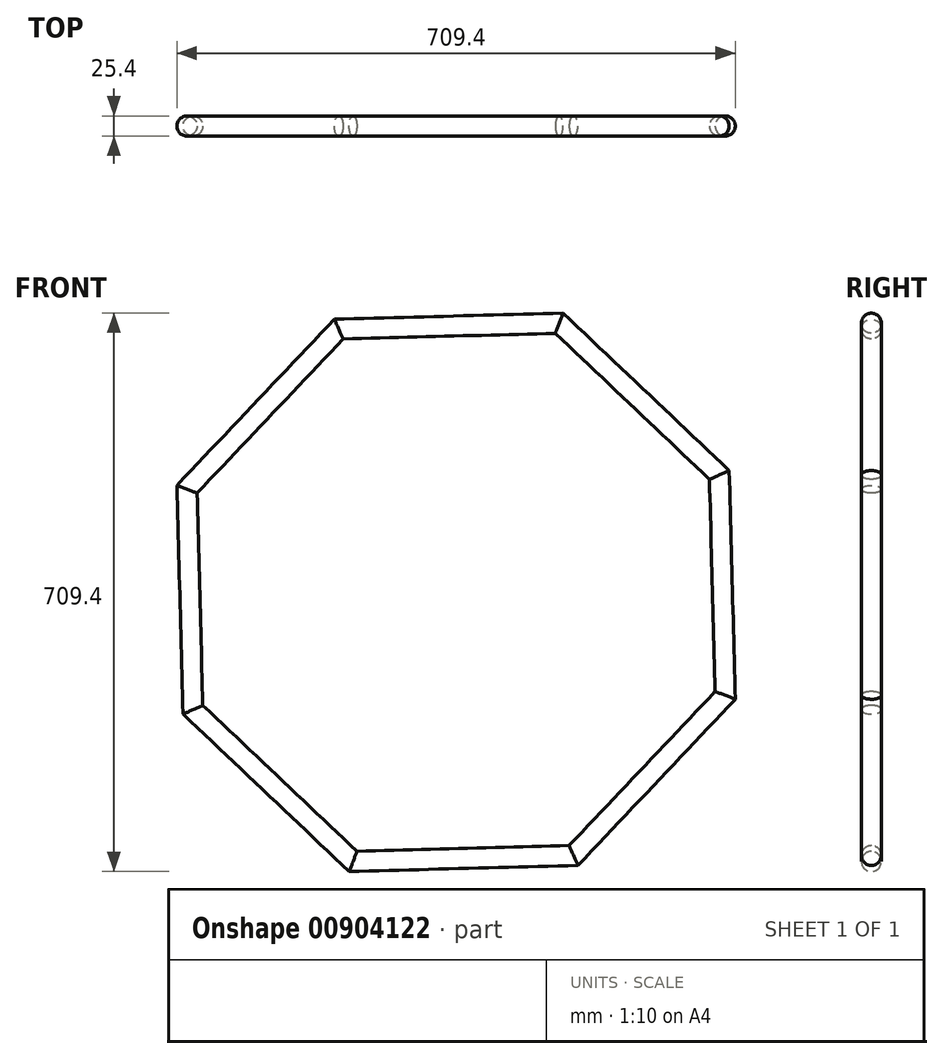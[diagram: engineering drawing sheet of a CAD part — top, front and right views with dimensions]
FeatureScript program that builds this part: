
annotation { "Feature Type Name" : "Feature", "Feature Type Description" : "" }
export const myFeature = defineFeature(function(context is Context, id is Id, definition is map)
    precondition{}
    {
        {
            var Q0;
            Q0=qCreatedBy(makeId("Front.planeOp"),FACE);
            var sketch = newSketch(context, id + "F0", { "sketchPlane" : qUnion([Q0])});
            skLineSegment(sketch, "E0.bottom", {"start": v(304.8, 304.8) * mm, "end": v(-304.8, 304.8) * mm});
            skLineSegment(sketch, "E0.top", {"start": v(304.8, -304.8) * mm, "end": v(-304.8, -304.8) * mm});
            skLineSegment(sketch, "E0.left", {"start": v(304.8, 304.8) * mm, "end": v(304.8, -304.8) * mm});
            skLineSegment(sketch, "E0.right", {"start": v(-304.8, 304.8) * mm, "end": v(-304.8, -304.8) * mm});
            skPoint(sketch, "E0.middle", {"position": v(0, 0) * mm});
            skCircle(sketch, "E1.cCircle", {"center": v(0, 0) * mm, "radius": 337.27 * mm, "construction": true});
            skLineSegment(sketch, "E1.0", {"start": v(333.4, 148.71) * mm, "end": v(340.9, -130.59) * mm});
            skLineSegment(sketch, "E1.1", {"start": v(340.9, -130.59) * mm, "end": v(148.71, -333.4) * mm});
            skLineSegment(sketch, "E1.2", {"start": v(148.71, -333.4) * mm, "end": v(-130.59, -340.9) * mm});
            skLineSegment(sketch, "E1.3", {"start": v(-130.59, -340.9) * mm, "end": v(-333.4, -148.71) * mm});
            skLineSegment(sketch, "E1.4", {"start": v(-333.4, -148.71) * mm, "end": v(-340.9, 130.59) * mm});
            skLineSegment(sketch, "E1.5", {"start": v(-340.9, 130.59) * mm, "end": v(-148.71, 333.4) * mm});
            skLineSegment(sketch, "E1.6", {"start": v(-148.71, 333.4) * mm, "end": v(130.59, 340.9) * mm});
            skLineSegment(sketch, "E1.7", {"start": v(130.59, 340.9) * mm, "end": v(333.4, 148.71) * mm});
            skPoint(sketch, "E1.0.midPoint", {"position": v(337.14, 9.06) * mm});
            skSolve(sketch);
        }
        {
            var Q0;
            Q0=sQuery(id+"F0.wireOp",EDGE,"E1.0");
            cPlane(context, id + "F1", {"entities" : qUnion([Q0]), "cplaneType" : CPlaneType.LINE_ANGLE, "offset" : 25.4 * mm, "angle" : 0 * degree, "width" : 152.4 * mm, "height" : 152.4 * mm});
        }
        {
            var Q0;
            Q0=qCreatedBy(id+"F1.planeOp",FACE);
            var sketch = newSketch(context, id + "F2", { "sketchPlane" : qUnion([Q0])});
            skLineSegment(sketch, "E2.bottom", {"start": v(-113.95, 32.5) * mm, "end": v(-50.67, 32.5) * mm});
            skLineSegment(sketch, "E2.top", {"start": v(-113.95, 77.91) * mm, "end": v(-50.67, 77.91) * mm});
            skLineSegment(sketch, "E2.left", {"start": v(-113.95, 32.5) * mm, "end": v(-113.95, 77.91) * mm});
            skLineSegment(sketch, "E2.right", {"start": v(-50.67, 32.5) * mm, "end": v(-50.67, 77.91) * mm});
            skPoint(sketch, "E2.middle", {"position": v(-82.31, 55.2) * mm});
            skSolve(sketch);
        }
        {
            var Q0;
            Q0=sQuery(id+"F2.wireOp",EDGE,"E2.top");
            cPlane(context, id + "F3", {"entities" : qUnion([Q0]), "cplaneType" : CPlaneType.LINE_ANGLE, "offset" : 25.4 * mm, "angle" : 0 * degree, "width" : 152.4 * mm, "height" : 152.4 * mm});
        }
        {
            var Q0;
            Q0=qCreatedBy(id+"F3.planeOp",FACE);
            var sketch = newSketch(context, id + "F4", { "sketchPlane" : qUnion([Q0])});
            skCircle(sketch, "E3", {"center": v(336.01, 0) * mm, "radius": 12.7 * mm});
            skSolve(sketch);
        }
        {
            var Q0;
            Q0=makeQuery(id+"F4.imprint","IMPRINT",FACE,{"disambiguationData":[TD([[makeQuery(id+"F4.imprint","IMPRINT",EDGE,{"derivedFrom":sQuery(id+"F4.wireOp",EDGE,"E3")}),1.0]])]});
            var Q1;
            Q1=sQuery(id+"F0.wireOp",EDGE,"E1.7");
            var Q2;
            Q2=sQuery(id+"F0.wireOp",EDGE,"E1.6");
            var Q3;
            Q3=sQuery(id+"F0.wireOp",EDGE,"E1.5");
            var Q4;
            Q4=sQuery(id+"F0.wireOp",EDGE,"E1.4");
            var Q5;
            Q5=sQuery(id+"F0.wireOp",EDGE,"E1.3");
            var Q6;
            Q6=sQuery(id+"F0.wireOp",EDGE,"E1.2");
            var Q7;
            Q7=sQuery(id+"F0.wireOp",EDGE,"E1.1");
            var Q8;
            Q8=sQuery(id+"F0.wireOp",EDGE,"E1.0");
            sweep(context, id + "F5", {"profiles" : qUnion([Q0]), "path" : qUnion([Q1, Q2, Q3, Q4, Q5, Q6, Q7, Q8])});
        }
    });
